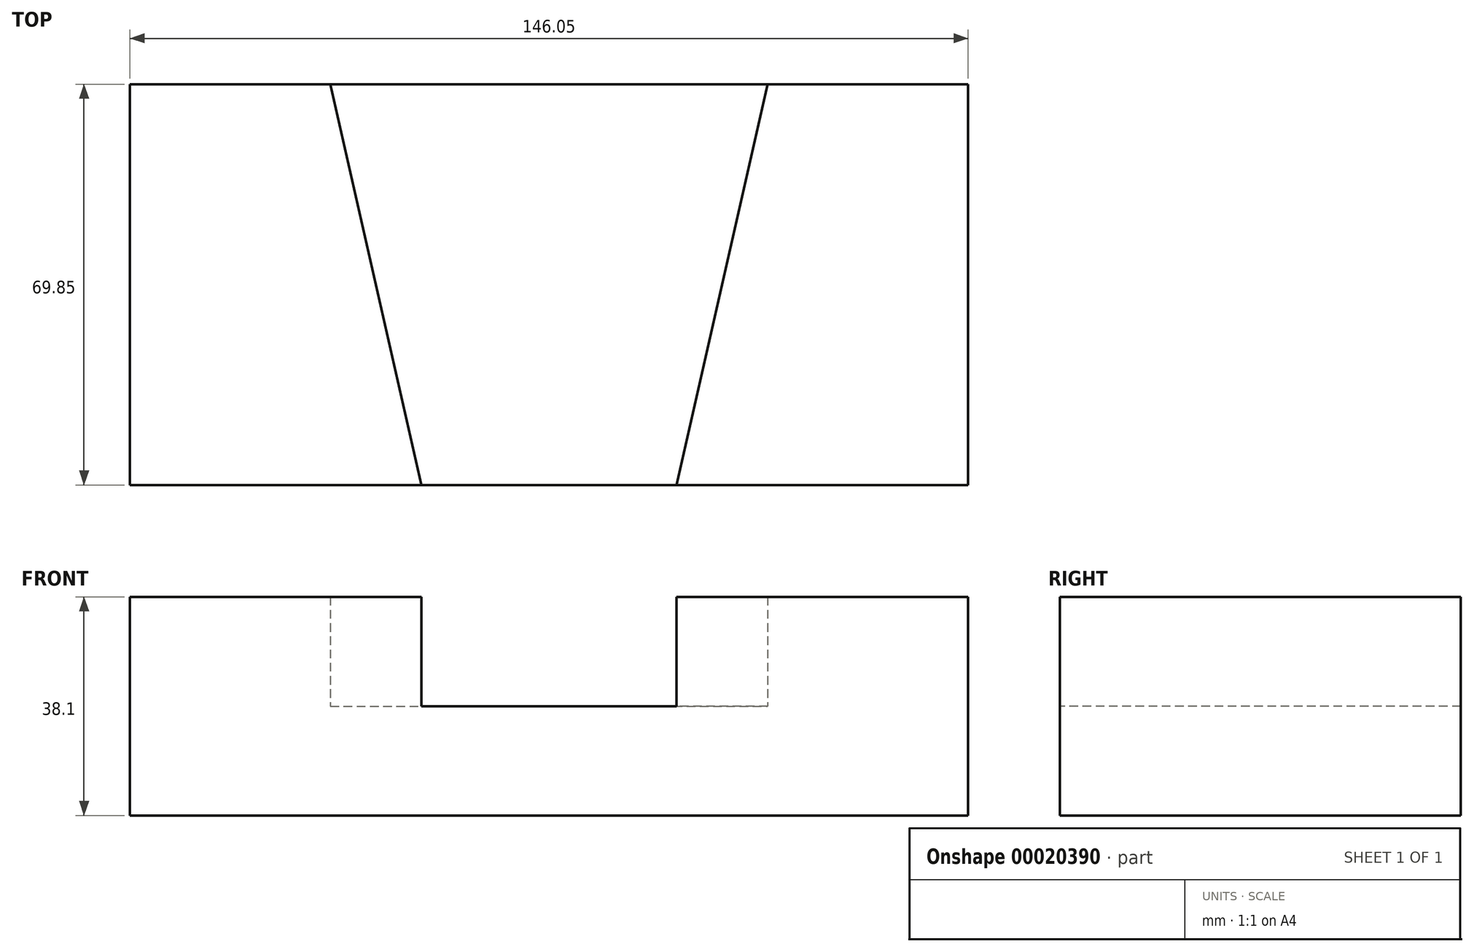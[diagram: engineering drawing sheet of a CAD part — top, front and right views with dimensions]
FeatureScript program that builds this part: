
annotation { "Feature Type Name" : "Feature", "Feature Type Description" : "" }
export const myFeature = defineFeature(function(context is Context, id is Id, definition is map)
    precondition{}
    {
        {
            var Q0;
            Q0=qCreatedBy(makeId("Front.planeOp"),FACE);
            var sketch = newSketch(context, id + "F0", { "sketchPlane" : qUnion([Q0])});
            skLineSegment(sketch, "E0.bottom", {"start": v(-93.5, 11.22) * mm, "end": v(52.55, 11.22) * mm});
            skLineSegment(sketch, "E0.top", {"start": v(-93.5, -7.83) * mm, "end": v(52.55, -7.83) * mm});
            skLineSegment(sketch, "E0.left", {"start": v(-93.5, 11.22) * mm, "end": v(-93.5, -7.83) * mm});
            skLineSegment(sketch, "E0.right", {"start": v(52.55, 11.22) * mm, "end": v(52.55, -7.83) * mm});
            skSolve(sketch);
        }
        {
            var Q0;
            Q0=makeQuery(id+"F0.imprint","IMPRINT",FACE,{"disambiguationData":[TD([[makeQuery(id+"F0.imprint","IMPRINT",EDGE,{"derivedFrom":sQuery(id+"F0.wireOp",EDGE,"E0.bottom")}),-1.0]])]});
            extrude(context, id + "F1", {"entities" : qUnion([Q0]), "depth" : 69.85 * mm});
        }
        {
            var Q0;
            Q0=makeQuery(id+"F1.opExtrude","SWEPT_FACE",FACE,{"disambiguationData":[OSD([sQuery(id+"F0.wireOp",EDGE,"E0.bottom")])]});
            var sketch = newSketch(context, id + "F2", { "sketchPlane" : qUnion([Q0])});
            skLineSegment(sketch, "E1", {"start": v(-93.5, 0) * mm, "end": v(-58.58, 0) * mm});
            skLineSegment(sketch, "E2", {"start": v(-93.5, -69.85) * mm, "end": v(-42.7, -69.85) * mm});
            skLineSegment(sketch, "E3", {"start": v(52.55, 0) * mm, "end": v(17.62, 0) * mm});
            skLineSegment(sketch, "E4", {"start": v(52.55, -69.85) * mm, "end": v(1.75, -69.85) * mm});
            skLineSegment(sketch, "E5", {"start": v(-93.5, 0) * mm, "end": v(-93.5, -69.85) * mm});
            skLineSegment(sketch, "E6", {"start": v(-58.58, 0) * mm, "end": v(-42.7, -69.85) * mm});
            skSolve(sketch);
        }
        {
            var Q0;
            Q0=makeQuery(id+"F2.imprint","IMPRINT",FACE,{"disambiguationData":[TD([[makeQuery(id+"F2.imprint","IMPRINT",EDGE,{"derivedFrom":sQuery(id+"F2.wireOp",EDGE,"E1")}),-1.0]])]});
            extrude(context, id + "F3", {"entities" : qUnion([Q0]), "operationType" : NewBodyOperationType.ADD, "depth" : 19.05 * mm});
        }
        {
            var Q0;
            Q0=makeQuery(id+"F1.opExtrude","SWEPT_FACE",FACE,{"disambiguationData":[OSD([sQuery(id+"F0.wireOp",EDGE,"E0.bottom")])]});
            var sketch = newSketch(context, id + "F4", { "sketchPlane" : qUnion([Q0])});
            skLineSegment(sketch, "E7", {"start": v(52.55, 0) * mm, "end": v(17.62, 0) * mm});
            skLineSegment(sketch, "E8", {"start": v(52.55, -69.85) * mm, "end": v(1.75, -69.85) * mm});
            skLineSegment(sketch, "E9", {"start": v(17.62, 0) * mm, "end": v(1.75, -69.85) * mm});
            skSolve(sketch);
        }
        {
            var Q0;
            Q0=makeQuery(id+"F4.imprint","IMPRINT",FACE,{"disambiguationData":[TD([[makeQuery(id+"F4.imprint","IMPRINT",EDGE,{"derivedFrom":sQuery(id+"F4.wireOp",EDGE,"E7")}),-1.0]])]});
            extrude(context, id + "F5", {"entities" : qUnion([Q0]), "operationType" : NewBodyOperationType.ADD, "depth" : 19.05 * mm});
        }
    });
